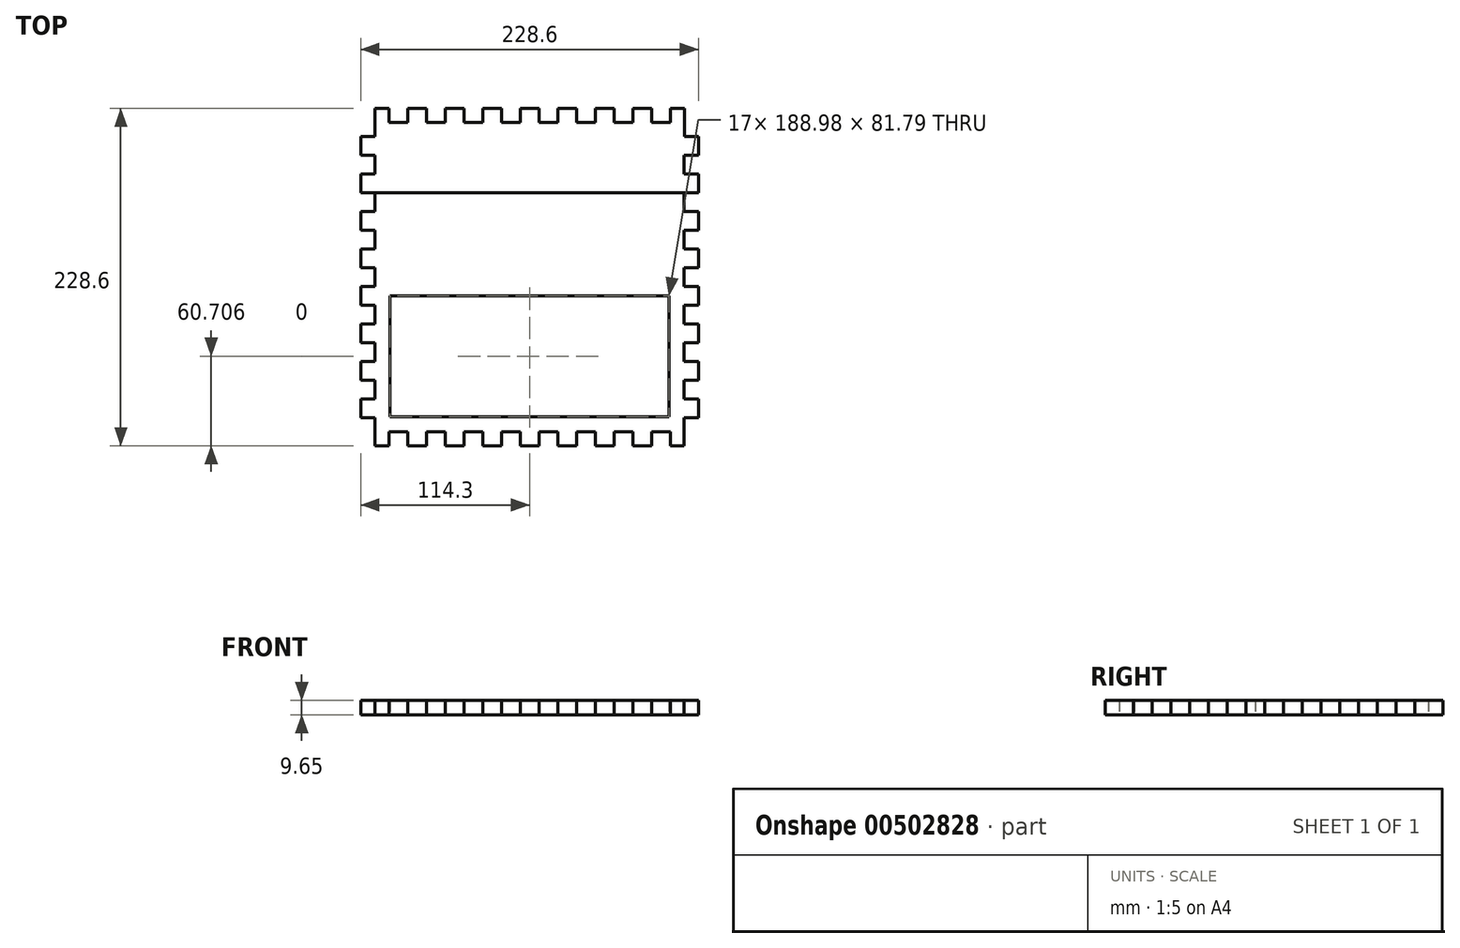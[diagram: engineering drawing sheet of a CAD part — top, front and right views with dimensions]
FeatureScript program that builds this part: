
annotation { "Feature Type Name" : "Feature", "Feature Type Description" : "" }
export const myFeature = defineFeature(function(context is Context, id is Id, definition is map)
    precondition{}
    {
        {
            var Q0;
            Q0=qCreatedBy(makeId("Top.planeOp"),FACE);
            var sketch = newSketch(context, id + "F0", { "sketchPlane" : qUnion([Q0])});
            skLineSegment(sketch, "E0.bottom", {"start": v(9.65, 0) * mm, "end": v(19.05, 0) * mm});
            skLineSegment(sketch, "E0.left", {"start": v(0, -19.05) * mm, "end": v(0, -31.75) * mm});
            skLineSegment(sketch, "E1", {"start": v(0, -19.05) * mm, "end": v(9.65, -19.05) * mm});
            skLineSegment(sketch, "E2", {"start": v(9.65, 0) * mm, "end": v(9.65, -19.05) * mm});
            skPoint(sketch, "E3.orphan", {"position": v(0, 0) * mm});
            skLineSegment(sketch, "E4", {"start": v(19.05, 0) * mm, "end": v(19.05, -9.65) * mm});
            skLineSegment(sketch, "E5", {"start": v(19.05, -9.65) * mm, "end": v(31.75, -9.65) * mm});
            skLineSegment(sketch, "E6", {"start": v(31.75, -9.65) * mm, "end": v(31.75, 0) * mm});
            skLineSegment(sketch, "E7", {"start": v(31.75, 0) * mm, "end": v(44.45, 0) * mm});
            skLineSegment(sketch, "E8", {"start": v(44.45, 0) * mm, "end": v(44.45, -9.65) * mm});
            skLineSegment(sketch, "E9", {"start": v(44.45, -9.65) * mm, "end": v(57.15, -9.65) * mm});
            skLineSegment(sketch, "E10", {"start": v(57.15, -9.65) * mm, "end": v(57.15, 0) * mm});
            skLineSegment(sketch, "E11", {"start": v(57.15, 0) * mm, "end": v(69.85, 0) * mm});
            skLineSegment(sketch, "E12", {"start": v(69.85, 0) * mm, "end": v(69.85, -9.65) * mm});
            skLineSegment(sketch, "E13", {"start": v(69.85, -9.65) * mm, "end": v(82.55, -9.65) * mm});
            skLineSegment(sketch, "E14", {"start": v(82.55, -9.65) * mm, "end": v(82.55, 0) * mm});
            skLineSegment(sketch, "E15.trimOffspring", {"start": v(82.55, 0) * mm, "end": v(95.25, 0) * mm});
            skLineSegment(sketch, "E16", {"start": v(95.25, 0) * mm, "end": v(95.25, -9.65) * mm});
            skLineSegment(sketch, "E17", {"start": v(95.25, -9.65) * mm, "end": v(107.95, -9.65) * mm});
            skLineSegment(sketch, "E18", {"start": v(107.95, -9.65) * mm, "end": v(107.95, 0) * mm});
            skLineSegment(sketch, "E19", {"start": v(107.95, 0) * mm, "end": v(120.65, 0) * mm});
            skLineSegment(sketch, "E20", {"start": v(120.65, 0) * mm, "end": v(120.65, -9.65) * mm});
            skLineSegment(sketch, "E21", {"start": v(120.65, -9.65) * mm, "end": v(133.35, -9.65) * mm});
            skLineSegment(sketch, "E22", {"start": v(133.35, -9.65) * mm, "end": v(133.35, 0) * mm});
            skLineSegment(sketch, "E23", {"start": v(133.35, 0) * mm, "end": v(146.05, 0) * mm});
            skLineSegment(sketch, "E24", {"start": v(146.05, 0) * mm, "end": v(146.05, -9.65) * mm});
            skLineSegment(sketch, "E25", {"start": v(146.05, -9.65) * mm, "end": v(158.75, -9.65) * mm});
            skLineSegment(sketch, "E26", {"start": v(158.75, -9.65) * mm, "end": v(158.75, 0) * mm});
            skLineSegment(sketch, "E27.trimOffspring", {"start": v(158.75, 0) * mm, "end": v(171.45, 0) * mm});
            skLineSegment(sketch, "E28", {"start": v(171.45, 0) * mm, "end": v(171.45, -9.65) * mm});
            skLineSegment(sketch, "E29", {"start": v(171.45, -9.65) * mm, "end": v(184.15, -9.65) * mm});
            skLineSegment(sketch, "E30", {"start": v(184.15, -9.65) * mm, "end": v(184.15, 0) * mm});
            skLineSegment(sketch, "E31", {"start": v(184.15, 0) * mm, "end": v(196.85, 0) * mm});
            skLineSegment(sketch, "E32", {"start": v(196.85, 0) * mm, "end": v(196.85, -9.65) * mm});
            skLineSegment(sketch, "E33", {"start": v(196.85, -9.65) * mm, "end": v(209.55, -9.65) * mm});
            skLineSegment(sketch, "E34", {"start": v(209.55, -9.65) * mm, "end": v(209.55, 0) * mm});
            skLineSegment(sketch, "E35.trimOffspring", {"start": v(209.55, 0) * mm, "end": v(219.07, 0) * mm});
            skLineSegment(sketch, "E36", {"start": v(219.07, 0) * mm, "end": v(219.07, -19.05) * mm});
            skLineSegment(sketch, "E37", {"start": v(219.08, -19.05) * mm, "end": v(228.73, -19.05) * mm});
            skPoint(sketch, "E38.orphan", {"position": v(228.6, 0) * mm});
            skLineSegment(sketch, "E39", {"start": v(0, -31.75) * mm, "end": v(9.65, -31.75) * mm});
            skLineSegment(sketch, "E40", {"start": v(9.65, -31.75) * mm, "end": v(9.65, -44.45) * mm});
            skLineSegment(sketch, "E41", {"start": v(9.65, -44.45) * mm, "end": v(0, -44.45) * mm});
            skLineSegment(sketch, "E42", {"start": v(0, -44.45) * mm, "end": v(0, -57.15) * mm});
            skLineSegment(sketch, "E43", {"start": v(0, -57.15) * mm, "end": v(9.65, -57.15) * mm});
            skLineSegment(sketch, "E44", {"start": v(9.65, -57.15) * mm, "end": v(9.65, -69.85) * mm});
            skLineSegment(sketch, "E45", {"start": v(9.65, -69.85) * mm, "end": v(0, -69.85) * mm});
            skLineSegment(sketch, "E46.trimOffspring", {"start": v(0, -69.85) * mm, "end": v(0, -82.55) * mm});
            skLineSegment(sketch, "E47", {"start": v(0, -82.55) * mm, "end": v(9.65, -82.55) * mm});
            skLineSegment(sketch, "E48", {"start": v(9.65, -82.55) * mm, "end": v(9.65, -95.25) * mm});
            skLineSegment(sketch, "E49", {"start": v(9.65, -95.25) * mm, "end": v(0, -95.25) * mm});
            skLineSegment(sketch, "E50", {"start": v(0, -95.25) * mm, "end": v(0, -107.95) * mm});
            skLineSegment(sketch, "E51", {"start": v(0, -107.95) * mm, "end": v(9.65, -107.95) * mm});
            skLineSegment(sketch, "E52", {"start": v(9.65, -107.95) * mm, "end": v(9.65, -120.65) * mm});
            skLineSegment(sketch, "E53", {"start": v(9.65, -120.65) * mm, "end": v(0, -120.65) * mm});
            skLineSegment(sketch, "E54", {"start": v(0, -120.65) * mm, "end": v(0, -133.35) * mm});
            skLineSegment(sketch, "E55", {"start": v(0, -133.35) * mm, "end": v(9.65, -133.35) * mm});
            skLineSegment(sketch, "E56", {"start": v(9.65, -133.35) * mm, "end": v(9.65, -146.05) * mm});
            skLineSegment(sketch, "E57", {"start": v(9.65, -146.05) * mm, "end": v(0, -146.05) * mm});
            skLineSegment(sketch, "E58.trimOffspring", {"start": v(0, -146.05) * mm, "end": v(0, -158.75) * mm});
            skLineSegment(sketch, "E59", {"start": v(0, -158.75) * mm, "end": v(9.65, -158.75) * mm});
            skLineSegment(sketch, "E60", {"start": v(9.65, -158.75) * mm, "end": v(9.65, -171.45) * mm});
            skLineSegment(sketch, "E61", {"start": v(9.65, -171.45) * mm, "end": v(0, -171.45) * mm});
            skLineSegment(sketch, "E62", {"start": v(0, -171.45) * mm, "end": v(0, -184.15) * mm});
            skLineSegment(sketch, "E63", {"start": v(0, -184.15) * mm, "end": v(9.65, -184.15) * mm});
            skLineSegment(sketch, "E64", {"start": v(9.65, -184.15) * mm, "end": v(9.65, -196.85) * mm});
            skLineSegment(sketch, "E65", {"start": v(9.65, -196.85) * mm, "end": v(0, -196.85) * mm});
            skLineSegment(sketch, "E66.trimOffspring", {"start": v(0, -196.85) * mm, "end": v(0, -209.55) * mm});
            skLineSegment(sketch, "E67", {"start": v(0, -209.55) * mm, "end": v(9.65, -209.55) * mm});
            skLineSegment(sketch, "E68", {"start": v(9.65, -209.55) * mm, "end": v(9.65, -228.6) * mm});
            skPoint(sketch, "E69.orphan", {"position": v(0, -228.6) * mm});
            skLineSegment(sketch, "E70", {"start": v(114.3, 0) * mm, "end": v(114.3, -42.4) * mm, "construction": true});
            skLineSegment(sketch, "E71.MirrorCS", {"start": v(228.6, -19.05) * mm, "end": v(228.6, -31.75) * mm});
            skLineSegment(sketch, "E72.MirrorCS", {"start": v(228.6, -31.75) * mm, "end": v(218.95, -31.75) * mm});
            skLineSegment(sketch, "E73.MirrorCS", {"start": v(218.95, -31.75) * mm, "end": v(218.95, -44.45) * mm});
            skLineSegment(sketch, "E74.MirrorCS", {"start": v(218.95, -44.45) * mm, "end": v(228.6, -44.45) * mm});
            skLineSegment(sketch, "E75.MirrorCS", {"start": v(228.6, -44.45) * mm, "end": v(228.6, -57.15) * mm});
            skLineSegment(sketch, "E76.MirrorCS", {"start": v(228.6, -57.15) * mm, "end": v(218.95, -57.15) * mm});
            skLineSegment(sketch, "E77.MirrorCS", {"start": v(218.95, -57.15) * mm, "end": v(218.95, -69.85) * mm});
            skLineSegment(sketch, "E78.MirrorCS", {"start": v(218.95, -69.85) * mm, "end": v(228.6, -69.85) * mm});
            skLineSegment(sketch, "E79.MirrorCS", {"start": v(228.6, -69.85) * mm, "end": v(228.6, -82.55) * mm});
            skLineSegment(sketch, "E80.MirrorCS", {"start": v(228.6, -82.55) * mm, "end": v(218.95, -82.55) * mm});
            skLineSegment(sketch, "E81.MirrorCS", {"start": v(218.95, -82.55) * mm, "end": v(218.95, -95.25) * mm});
            skLineSegment(sketch, "E82.MirrorCS", {"start": v(218.95, -95.25) * mm, "end": v(228.6, -95.25) * mm});
            skLineSegment(sketch, "E83.MirrorCS", {"start": v(228.6, -95.25) * mm, "end": v(228.6, -107.95) * mm});
            skLineSegment(sketch, "E84.MirrorCS", {"start": v(228.6, -107.95) * mm, "end": v(218.95, -107.95) * mm});
            skLineSegment(sketch, "E85.MirrorCS", {"start": v(218.95, -107.95) * mm, "end": v(218.95, -120.65) * mm});
            skLineSegment(sketch, "E86.MirrorCS", {"start": v(218.95, -120.65) * mm, "end": v(228.6, -120.65) * mm});
            skLineSegment(sketch, "E87.MirrorCS", {"start": v(228.6, -120.65) * mm, "end": v(228.6, -133.35) * mm});
            skLineSegment(sketch, "E88.MirrorCS", {"start": v(228.6, -133.35) * mm, "end": v(218.95, -133.35) * mm});
            skLineSegment(sketch, "E89.MirrorCS", {"start": v(218.95, -133.35) * mm, "end": v(218.95, -146.05) * mm});
            skLineSegment(sketch, "E90.MirrorCS", {"start": v(218.95, -146.05) * mm, "end": v(228.6, -146.05) * mm});
            skLineSegment(sketch, "E91.MirrorCS", {"start": v(228.6, -146.05) * mm, "end": v(228.6, -158.75) * mm});
            skLineSegment(sketch, "E92.MirrorCS", {"start": v(228.6, -158.75) * mm, "end": v(218.95, -158.75) * mm});
            skLineSegment(sketch, "E93.MirrorCS", {"start": v(218.95, -158.75) * mm, "end": v(218.95, -171.45) * mm});
            skLineSegment(sketch, "E94.MirrorCS", {"start": v(218.95, -171.45) * mm, "end": v(228.6, -171.45) * mm});
            skLineSegment(sketch, "E95.MirrorCS", {"start": v(228.6, -171.45) * mm, "end": v(228.6, -184.15) * mm});
            skLineSegment(sketch, "E96.MirrorCS", {"start": v(228.6, -184.15) * mm, "end": v(218.95, -184.15) * mm});
            skLineSegment(sketch, "E97.MirrorCS", {"start": v(218.95, -184.15) * mm, "end": v(218.95, -196.85) * mm});
            skLineSegment(sketch, "E98.MirrorCS", {"start": v(218.95, -196.85) * mm, "end": v(228.6, -196.85) * mm});
            skLineSegment(sketch, "E99.MirrorCS", {"start": v(228.6, -196.85) * mm, "end": v(228.6, -209.55) * mm});
            skLineSegment(sketch, "E100.MirrorCS", {"start": v(228.6, -209.55) * mm, "end": v(218.95, -209.55) * mm});
            skLineSegment(sketch, "E101.MirrorCS", {"start": v(218.95, -209.55) * mm, "end": v(218.95, -228.6) * mm});
            skLineSegment(sketch, "E102", {"start": v(218.95, -114.3) * mm, "end": v(145.5, -114.3) * mm, "construction": true});
            skLineSegment(sketch, "E103.MirrorCS", {"start": v(209.55, -228.6) * mm, "end": v(219.07, -228.6) * mm});
            skLineSegment(sketch, "E104.MirrorCS", {"start": v(209.55, -218.95) * mm, "end": v(209.55, -228.6) * mm});
            skLineSegment(sketch, "E105.MirrorCS", {"start": v(196.85, -218.95) * mm, "end": v(209.55, -218.95) * mm});
            skLineSegment(sketch, "E106.MirrorCS", {"start": v(196.85, -228.6) * mm, "end": v(196.85, -218.95) * mm});
            skLineSegment(sketch, "E107.MirrorCS", {"start": v(184.15, -228.6) * mm, "end": v(196.85, -228.6) * mm});
            skLineSegment(sketch, "E108.MirrorCS", {"start": v(184.15, -218.95) * mm, "end": v(184.15, -228.6) * mm});
            skLineSegment(sketch, "E109.MirrorCS", {"start": v(171.45, -218.95) * mm, "end": v(184.15, -218.95) * mm});
            skLineSegment(sketch, "E110.MirrorCS", {"start": v(171.45, -228.6) * mm, "end": v(171.45, -218.95) * mm});
            skLineSegment(sketch, "E111.MirrorCS", {"start": v(158.75, -228.6) * mm, "end": v(171.45, -228.6) * mm});
            skLineSegment(sketch, "E112.MirrorCS", {"start": v(158.75, -218.95) * mm, "end": v(158.75, -228.6) * mm});
            skLineSegment(sketch, "E113.MirrorCS", {"start": v(146.05, -218.95) * mm, "end": v(158.75, -218.95) * mm});
            skLineSegment(sketch, "E114.MirrorCS", {"start": v(146.05, -228.6) * mm, "end": v(146.05, -218.95) * mm});
            skLineSegment(sketch, "E115.MirrorCS", {"start": v(133.35, -228.6) * mm, "end": v(146.05, -228.6) * mm});
            skLineSegment(sketch, "E116.MirrorCS", {"start": v(133.35, -218.95) * mm, "end": v(133.35, -228.6) * mm});
            skLineSegment(sketch, "E117.MirrorCS", {"start": v(120.65, -218.95) * mm, "end": v(133.35, -218.95) * mm});
            skLineSegment(sketch, "E118.MirrorCS", {"start": v(120.65, -228.6) * mm, "end": v(120.65, -218.95) * mm});
            skLineSegment(sketch, "E119.MirrorCS", {"start": v(107.95, -228.6) * mm, "end": v(120.65, -228.6) * mm});
            skLineSegment(sketch, "E120.MirrorCS", {"start": v(107.95, -218.95) * mm, "end": v(107.95, -228.6) * mm});
            skLineSegment(sketch, "E121.MirrorCS", {"start": v(95.25, -218.95) * mm, "end": v(107.95, -218.95) * mm});
            skLineSegment(sketch, "E122.MirrorCS", {"start": v(95.25, -228.6) * mm, "end": v(95.25, -218.95) * mm});
            skLineSegment(sketch, "E123.MirrorCS", {"start": v(82.55, -228.6) * mm, "end": v(95.25, -228.6) * mm});
            skLineSegment(sketch, "E124.MirrorCS", {"start": v(82.55, -218.95) * mm, "end": v(82.55, -228.6) * mm});
            skLineSegment(sketch, "E125.MirrorCS", {"start": v(69.85, -218.95) * mm, "end": v(82.55, -218.95) * mm});
            skLineSegment(sketch, "E126.MirrorCS", {"start": v(69.85, -228.6) * mm, "end": v(69.85, -218.95) * mm});
            skLineSegment(sketch, "E127.MirrorCS", {"start": v(57.15, -228.6) * mm, "end": v(69.85, -228.6) * mm});
            skLineSegment(sketch, "E128.MirrorCS", {"start": v(57.15, -218.95) * mm, "end": v(57.15, -228.6) * mm});
            skLineSegment(sketch, "E129.MirrorCS", {"start": v(44.45, -218.95) * mm, "end": v(57.15, -218.95) * mm});
            skLineSegment(sketch, "E130.MirrorCS", {"start": v(44.45, -228.6) * mm, "end": v(44.45, -218.95) * mm});
            skLineSegment(sketch, "E131.MirrorCS", {"start": v(31.75, -228.6) * mm, "end": v(44.45, -228.6) * mm});
            skLineSegment(sketch, "E132.MirrorCS", {"start": v(31.75, -218.95) * mm, "end": v(31.75, -228.6) * mm});
            skLineSegment(sketch, "E133.MirrorCS", {"start": v(19.05, -218.95) * mm, "end": v(31.75, -218.95) * mm});
            skLineSegment(sketch, "E134.MirrorCS", {"start": v(19.05, -228.6) * mm, "end": v(19.05, -218.95) * mm});
            skLineSegment(sketch, "E135.MirrorCS", {"start": v(9.65, -228.6) * mm, "end": v(19.05, -228.6) * mm});
            skLineSegment(sketch, "E136", {"start": v(9.65, -57.15) * mm, "end": v(218.95, -57.15) * mm});
            skLineSegment(sketch, "E137.bottom", {"start": v(19.81, -127) * mm, "end": v(208.79, -127) * mm});
            skLineSegment(sketch, "E137.top", {"start": v(19.81, -208.79) * mm, "end": v(208.79, -208.79) * mm});
            skLineSegment(sketch, "E137.left", {"start": v(19.81, -127) * mm, "end": v(19.81, -208.79) * mm});
            skLineSegment(sketch, "E137.right", {"start": v(208.79, -127) * mm, "end": v(208.79, -208.79) * mm});
            skSolve(sketch);
        }
        {
            var Q0;
            Q0=makeQuery(id+"F0.imprint","IMPRINT",FACE,{"disambiguationData":[TD([[makeQuery(id+"F0.imprint","IMPRINT",EDGE,{"derivedFrom":sQuery(id+"F0.wireOp",EDGE,"E1")}),-1.0]])]});
            extrude(context, id + "F1", {"entities" : qUnion([Q0]), "depth" : 9.65 * mm});
        }
        {
            var Q0;
            Q0=makeQuery(id+"F0.imprint","IMPRINT",FACE,{"disambiguationData":[TD([[makeQuery(id+"F0.imprint","IMPRINT",EDGE,{"derivedFrom":sQuery(id+"F0.wireOp",EDGE,"E44")}),1.0]])]});
            extrude(context, id + "F2", {"entities" : qUnion([Q0]), "depth" : 9.65 * mm});
        }
    });
